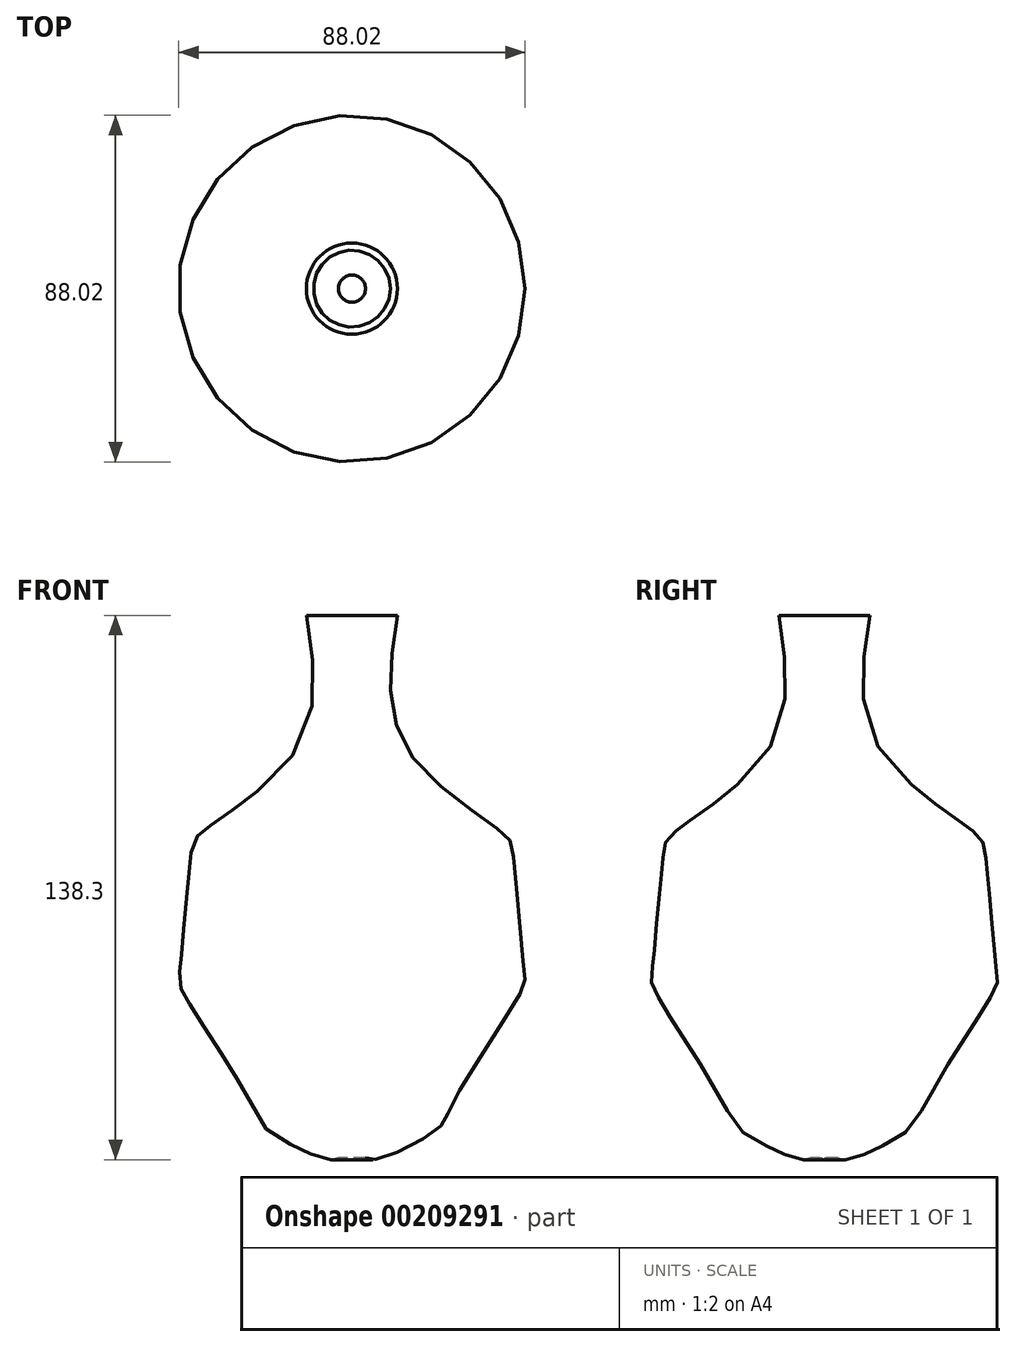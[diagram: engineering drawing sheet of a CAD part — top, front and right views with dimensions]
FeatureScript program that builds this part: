
annotation { "Feature Type Name" : "Feature", "Feature Type Description" : "" }
export const myFeature = defineFeature(function(context is Context, id is Id, definition is map)
    precondition{}
    {
        {
            var Q0;
            Q0=qCreatedBy(makeId("Right.planeOp"),FACE);
            var sketch = newSketch(context, id + "F0", { "sketchPlane" : qUnion([Q0])});
            skFitSpline(sketch, "E0", {"points": [v(11.57, 65.49) * mm, v(14.07, 31.41) * mm, v(38.45, 10.16) * mm, v(40.95, 4.53) * mm, v(43.76, -24.54) * mm, v(43.14, -29.85) * mm, v(25.32, -58.92) * mm, v(21.88, -64.86) * mm, v(6.56, -72.68) * mm, v(3.44, -72.36) * mm], "startDerivative": vector(-34.8, -223.35) * mm, "endDerivative": vector(-46.42, 19.52) * mm});
            skLineSegment(sketch, "E1", {"start": v(0, 75.8) * mm, "end": v(0, 93.62) * mm});
            skSolve(sketch);
        }
        {
            var Q0;
            Q0=sQuery(id+"F0.wireOp",EDGE,"E0");
            var Q1;
            Q1=sQuery(id+"F0.wireOp",EDGE,"E1");
            revolve(context, id + "F1", {"bodyType" : ToolBodyType.SURFACE, "surfaceEntities" : qUnion([Q0]), "axis" : qUnion([Q1]), "revolveType" : RevolveType.FULL});
        }
    });
